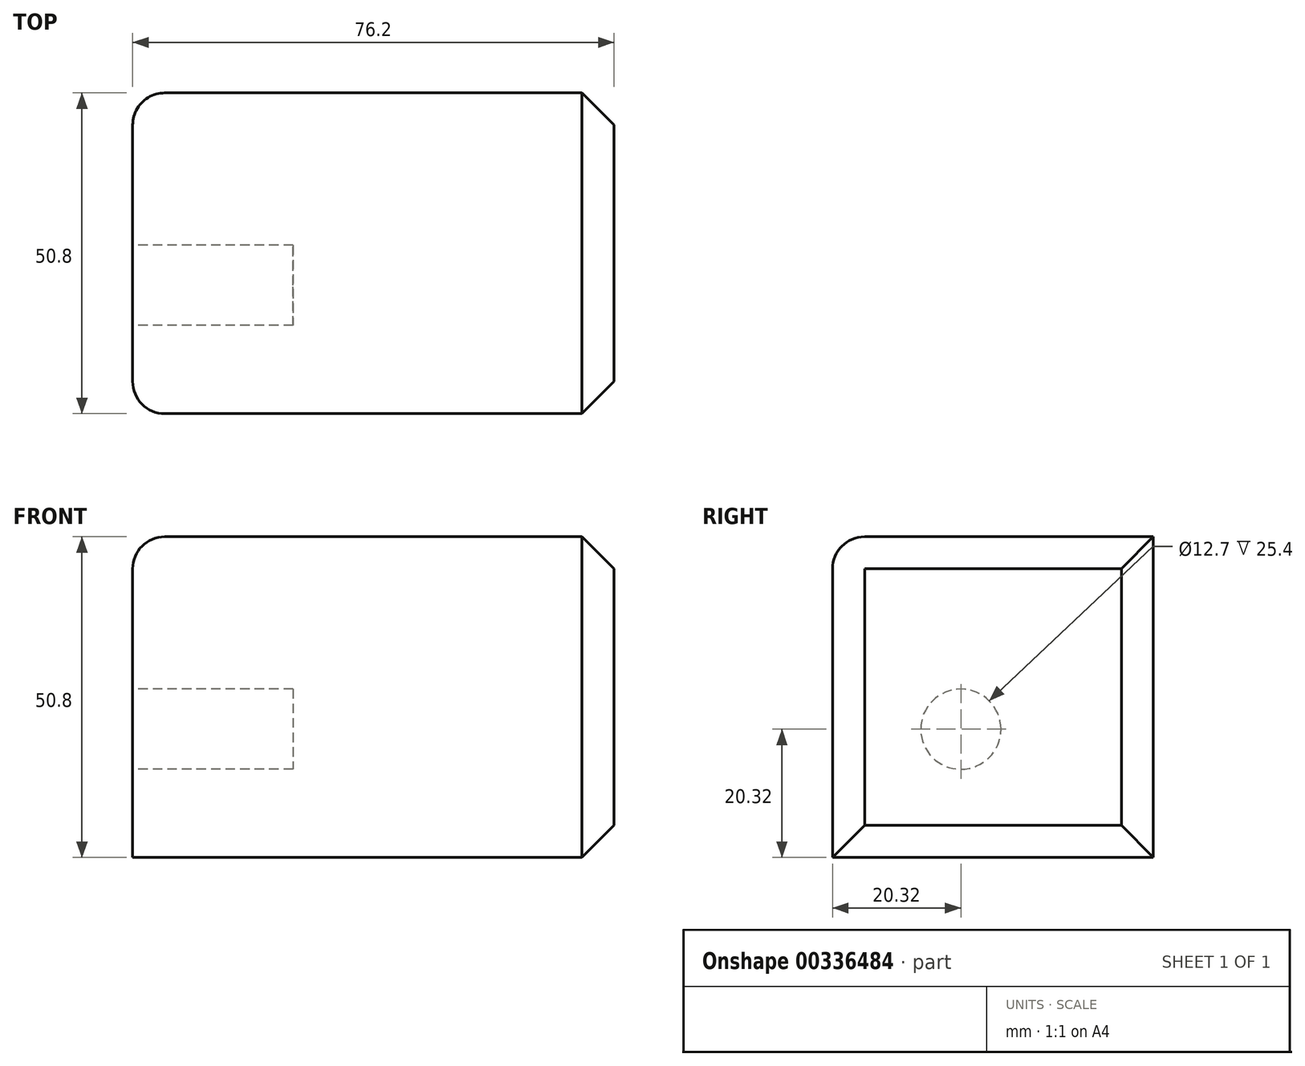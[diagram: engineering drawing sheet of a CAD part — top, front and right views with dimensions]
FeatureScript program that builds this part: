
annotation { "Feature Type Name" : "Feature", "Feature Type Description" : "" }
export const myFeature = defineFeature(function(context is Context, id is Id, definition is map)
    precondition{}
    {
        {
            var Q0;
            Q0=qCreatedBy(makeId("Front.planeOp"),FACE);
            var sketch = newSketch(context, id + "F0", { "sketchPlane" : qUnion([Q0])});
            skLineSegment(sketch, "E0", {"start": v(0, 0) * mm, "end": v(0, 50.8) * mm});
            skLineSegment(sketch, "E1", {"start": v(0, 50.8) * mm, "end": v(76.2, 50.8) * mm});
            skLineSegment(sketch, "E2", {"start": v(76.2, 50.8) * mm, "end": v(76.2, 0) * mm});
            skLineSegment(sketch, "E3", {"start": v(76.2, 0) * mm, "end": v(0, 0) * mm});
            skSolve(sketch);
        }
        {
            var Q0;
            Q0 = qSketchRegion(id + "F0", true);
            extrude(context, id + "F1", {"entities" : qUnion([Q0]), "depth" : 50.8 * mm});
        }
        {
            var Q0;
            Q0=makeQuery(id+"F1.opExtrude","SWEPT_EDGE",EDGE,{"disambiguationData":[OSD([sQuery(id+"F0.wireOp",EDGE,"E0"),sQuery(id+"F0.wireOp",EDGE,"E1")])]});
            var Q1;
            Q1=makeQuery(id+"F1.opExtrude","CAP_EDGE",EDGE,{"disambiguationData":[OSD([sQuery(id+"F0.wireOp",EDGE,"E1")])],"isStart":false});
            var Q2;
            Q2=makeQuery(id+"F1.opExtrude","CAP_EDGE",EDGE,{"disambiguationData":[OSD([sQuery(id+"F0.wireOp",EDGE,"E0")])],"isStart":false});
            var Q3;
            Q3=makeQuery(id+"F1.opExtrude","CAP_EDGE",EDGE,{"disambiguationData":[OSD([sQuery(id+"F0.wireOp",EDGE,"E0")])],"isStart":true});
            fillet(context, id + "F2", {"entities" : qUnion([Q0, Q1, Q2, Q3]), "radius" : 5.08 * mm, "tangentPropagation" : true, "allowEdgeOverflow" : false});
        }
        {
            var Q0;
            Q0=makeQuery(id+"F1.opExtrude","SWEPT_FACE",FACE,{"disambiguationData":[OSD([sQuery(id+"F0.wireOp",EDGE,"E0")])]});
            var sketch = newSketch(context, id + "F3", { "sketchPlane" : qUnion([Q0])});
            skCircle(sketch, "E4", {"center": v(30.48, 20.32) * mm, "radius": 6.35 * mm});
            skSolve(sketch);
        }
        {
            var Q0;
            Q0 = qSketchRegion(id + "F3", true);
            extrude(context, id + "F4", {"entities" : qUnion([Q0]), "operationType" : NewBodyOperationType.REMOVE, "oppositeDirection" : true, "depth" : 25.4 * mm, "hasSecondDirection" : true, "secondDirectionOppositeDirection" : false, "secondDirectionDepth" : 25.4 * mm});
        }
        {
            var Q0;
            Q0=makeQuery(id+"F1.opExtrude","CAP_EDGE",EDGE,{"disambiguationData":[OSD([sQuery(id+"F0.wireOp",EDGE,"E2")])],"isStart":false});
            var Q1;
            Q1=makeQuery(id+"F1.opExtrude","SWEPT_EDGE",EDGE,{"disambiguationData":[OSD([sQuery(id+"F0.wireOp",EDGE,"E2"),sQuery(id+"F0.wireOp",EDGE,"E3")])]});
            var Q2;
            Q2=makeQuery(id+"F1.opExtrude","CAP_EDGE",EDGE,{"disambiguationData":[OSD([sQuery(id+"F0.wireOp",EDGE,"E2")])],"isStart":true});
            chamfer(context, id + "F5", {"entities" : qUnion([Q0, Q1, Q2]), "width" : 5.08 * mm, "tangentPropagation" : true});
        }
    });
